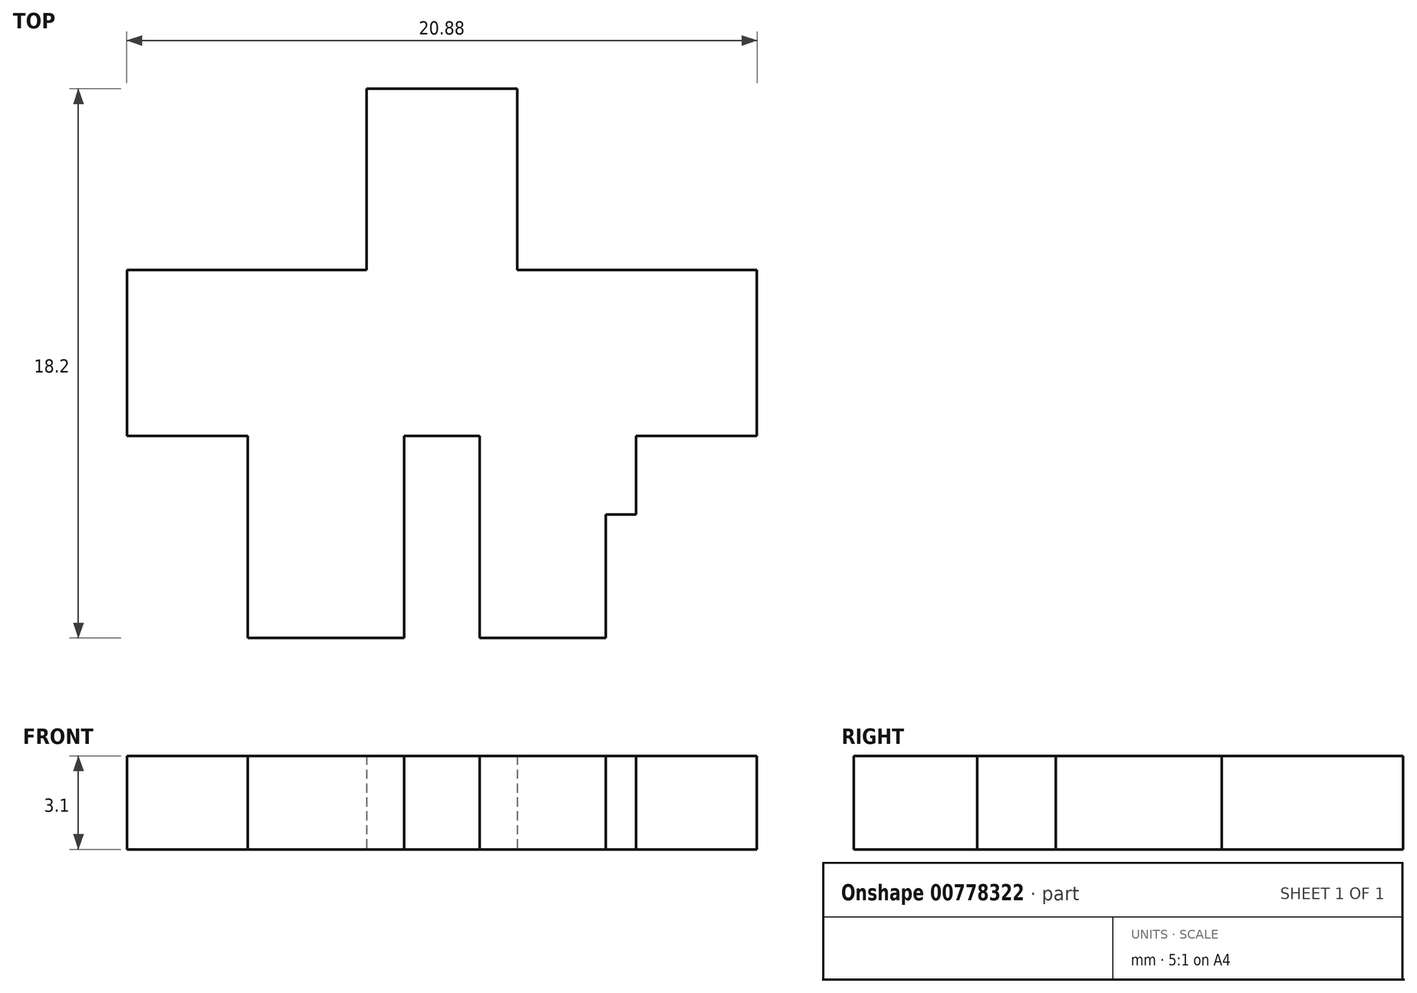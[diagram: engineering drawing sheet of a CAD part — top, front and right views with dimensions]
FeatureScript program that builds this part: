
annotation { "Feature Type Name" : "Feature", "Feature Type Description" : "" }
export const myFeature = defineFeature(function(context is Context, id is Id, definition is map)
    precondition{}
    {
        {
            var Q0;
            Q0=qCreatedBy(makeId("Top.planeOp"),FACE);
            var sketch = newSketch(context, id + "F0", { "sketchPlane" : qUnion([Q0])});
            skLineSegment(sketch, "E0.bottom", {"start": v(-2.5, 9.1) * mm, "end": v(2.5, 9.1) * mm});
            skLineSegment(sketch, "E0.top", {"start": v(-4.44, -9.1) * mm, "end": v(-1.25, -9.1) * mm});
            skLineSegment(sketch, "E0.left", {"start": v(-10.44, 3.1) * mm, "end": v(-10.44, -2.4) * mm});
            skLineSegment(sketch, "E0.right", {"start": v(10.44, 3.1) * mm, "end": v(10.44, -2.4) * mm});
            skPoint(sketch, "E0.middle", {"position": v(0, 0) * mm});
            skLineSegment(sketch, "E1", {"start": v(0, 9.1) * mm, "end": v(0, -9.1) * mm, "construction": true});
            skLineSegment(sketch, "E2.0", {"start": v(-2.5, 9.1) * mm, "end": v(-2.5, 3.1) * mm});
            skLineSegment(sketch, "E3.MirrorCS", {"start": v(2.5, 9.1) * mm, "end": v(2.5, 3.1) * mm});
            skLineSegment(sketch, "E4.0", {"start": v(-10.44, 3.1) * mm, "end": v(-2.5, 3.1) * mm});
            skLineSegment(sketch, "E5.0", {"start": v(-10.44, -2.4) * mm, "end": v(-6.44, -2.4) * mm});
            skLineSegment(sketch, "E6.0", {"start": v(6.44, -2.4) * mm, "end": v(6.44, -5) * mm});
            skLineSegment(sketch, "E7.MirrorCS", {"start": v(-6.44, -2.4) * mm, "end": v(-6.44, -5) * mm});
            skLineSegment(sketch, "E8.0", {"start": v(-1.25, -2.4) * mm, "end": v(-1.25, -9.1) * mm});
            skLineSegment(sketch, "E9.MirrorCS", {"start": v(1.25, -2.4) * mm, "end": v(1.25, -9.1) * mm});
            skPoint(sketch, "E10.orphan", {"position": v(-10.43, -9.1) * mm});
            skPoint(sketch, "E11.orphan", {"position": v(10.44, -9.1) * mm});
            skLineSegment(sketch, "E12.trimOffspring", {"start": v(1.25, -9.1) * mm, "end": v(4.44, -9.1) * mm});
            skPoint(sketch, "E13.orphan", {"position": v(-1.25, 9.1) * mm});
            skPoint(sketch, "E14.orphan", {"position": v(-6.44, 9.1) * mm});
            skPoint(sketch, "E15.orphan", {"position": v(-10.44, 9.1) * mm});
            skPoint(sketch, "E16.orphan", {"position": v(10.43, 9.1) * mm});
            skPoint(sketch, "E17.orphan", {"position": v(6.44, 9.1) * mm});
            skPoint(sketch, "E18.orphan", {"position": v(1.25, 9.1) * mm});
            skLineSegment(sketch, "E19.trimOffspring", {"start": v(2.5, 3.1) * mm, "end": v(10.44, 3.1) * mm});
            skPoint(sketch, "E20.trimOffspring.end.orphan", {"position": v(-2.5, -9.1) * mm});
            skPoint(sketch, "E21.orphan", {"position": v(2.5, -9.1) * mm});
            skLineSegment(sketch, "E22", {"start": v(-17.3, 0) * mm, "end": v(19.39, 0) * mm, "construction": true});
            skPoint(sketch, "E23.orphan", {"position": v(-6.43, -9.1) * mm});
            skPoint(sketch, "E24.orphan", {"position": v(6.44, -9.1) * mm});
            skPoint(sketch, "E25.orphan", {"position": v(-4.44, -2.4) * mm});
            skLineSegment(sketch, "E26.trimOffspring", {"start": v(-1.25, -2.4) * mm, "end": v(1.25, -2.4) * mm});
            skLineSegment(sketch, "E27.trimOffspring", {"start": v(5.43, -5) * mm, "end": v(6.44, -5) * mm});
            skLineSegment(sketch, "E28.trimOffspring", {"start": v(6.44, -2.4) * mm, "end": v(10.44, -2.4) * mm});
            skPoint(sketch, "E29.orphan", {"position": v(4.44, -2.4) * mm});
            skLineSegment(sketch, "E30", {"start": v(-6.44, -5) * mm, "end": v(-6.43, -9.1) * mm});
            skLineSegment(sketch, "E31", {"start": v(-4.44, -9.1) * mm, "end": v(-6.43, -9.1) * mm});
            skLineSegment(sketch, "E32.0", {"start": v(5.43, -5) * mm, "end": v(5.44, -9.1) * mm});
            skLineSegment(sketch, "E33", {"start": v(5.44, -9.1) * mm, "end": v(4.44, -9.1) * mm});
            skSolve(sketch);
        }
        {
            var Q0;
            Q0=makeQuery(id+"F0.imprint","IMPRINT",FACE,{"disambiguationData":[TD([[makeQuery(id+"F0.imprint","IMPRINT",EDGE,{"derivedFrom":sQuery(id+"F0.wireOp",EDGE,"E0.bottom")}),-1.0]])]});
            extrude(context, id + "F1", {"entities" : qUnion([Q0]), "depth" : 3.1 * mm, "offsetDistance" : 25 * mm});
        }
    });
